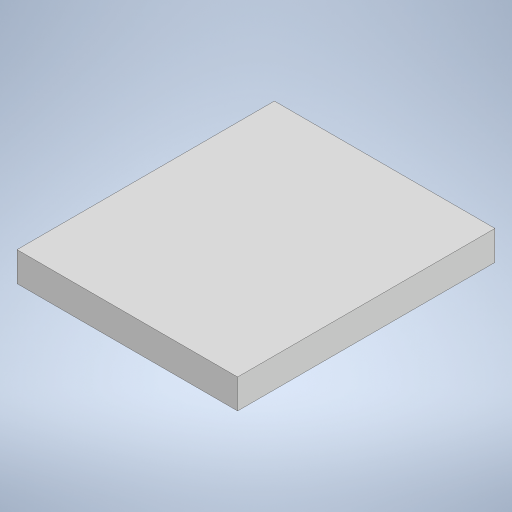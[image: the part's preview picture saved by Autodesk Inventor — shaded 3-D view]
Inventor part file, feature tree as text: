
AUTODESK INVENTOR PART (.ipt)
format: ipt  version: 2023 (Build 270158000, 158)  size: 193,024 bytes
history: native  units: mm
features: other x1, extrude x1, sketch x1
ambient origin geometry x8: Origin, YZ Plane, XZ Plane, XY Plane, X Axis, Y Axis, Z Axis, Center Point
bodies: Body1 (feature_tree)
feature tree (3):
  other  "Bryła1"
  extrude  "Wyciągnięcie proste1"  Depth=30.0mm
  sketch  "Szkic1"
